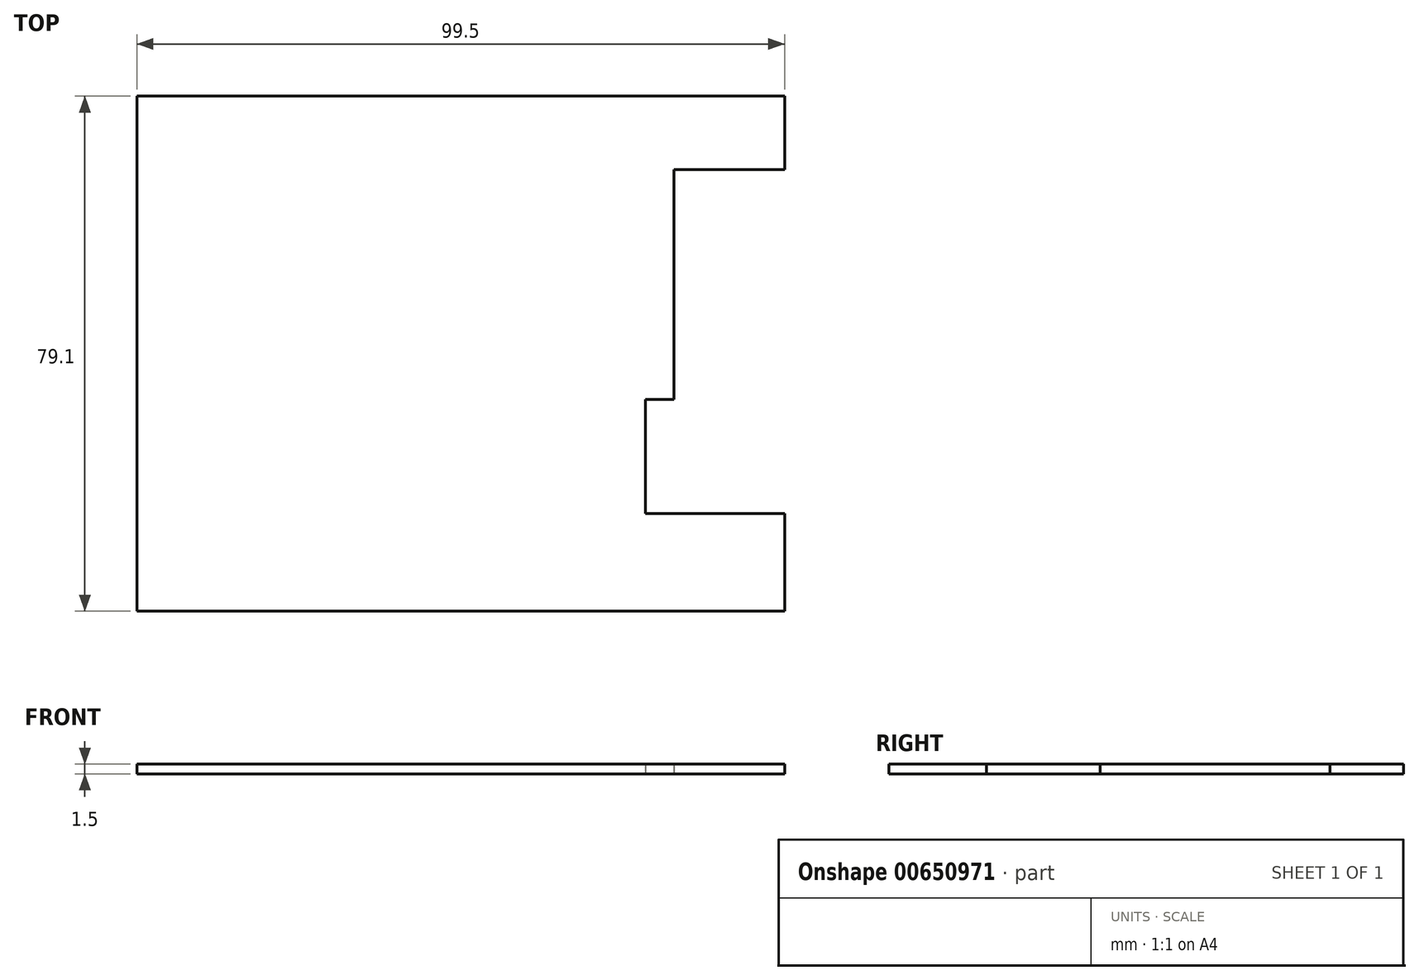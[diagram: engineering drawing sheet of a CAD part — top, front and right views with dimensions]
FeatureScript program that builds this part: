
annotation { "Feature Type Name" : "Feature", "Feature Type Description" : "" }
export const myFeature = defineFeature(function(context is Context, id is Id, definition is map)
    precondition{}
    {
        {
            var Q0;
            Q0=qCreatedBy(makeId("Top.planeOp"),FACE);
            var sketch = newSketch(context, id + "F0", { "sketchPlane" : qUnion([Q0])});
            skLineSegment(sketch, "E0.bottom", {"start": v(0, 0) * mm, "end": v(99.5, 0) * mm});
            skLineSegment(sketch, "E0.top", {"start": v(0, 79.1) * mm, "end": v(99.5, 79.1) * mm});
            skLineSegment(sketch, "E0.left", {"start": v(0, 0) * mm, "end": v(0, 79.1) * mm});
            skLineSegment(sketch, "E1.bottom", {"start": v(99.5, 15) * mm, "end": v(78.1, 15) * mm});
            skLineSegment(sketch, "E1.right", {"start": v(78.1, 15) * mm, "end": v(78.1, 32.5) * mm});
            skLineSegment(sketch, "E2.top", {"start": v(99.5, 67.8) * mm, "end": v(82.5, 67.8) * mm});
            skLineSegment(sketch, "E2.right", {"start": v(82.5, 32.5) * mm, "end": v(82.5, 67.8) * mm});
            skLineSegment(sketch, "E3", {"start": v(99.5, 0) * mm, "end": v(99.5, 15) * mm});
            skLineSegment(sketch, "E4", {"start": v(78.1, 32.5) * mm, "end": v(82.5, 32.5) * mm});
            skLineSegment(sketch, "E5", {"start": v(99.5, 67.8) * mm, "end": v(99.5, 79.1) * mm});
            skSolve(sketch);
        }
        {
            var Q0;
            Q0=makeQuery(id+"F0.imprint","IMPRINT",FACE,{"disambiguationData":[TD([[makeQuery(id+"F0.imprint","IMPRINT",EDGE,{"derivedFrom":sQuery(id+"F0.wireOp",EDGE,"E0.bottom")}),1.0]])]});
            extrude(context, id + "F1", {"entities" : qUnion([Q0]), "depth" : 1.5 * mm, "offsetDistance" : 25 * mm});
        }
    });
